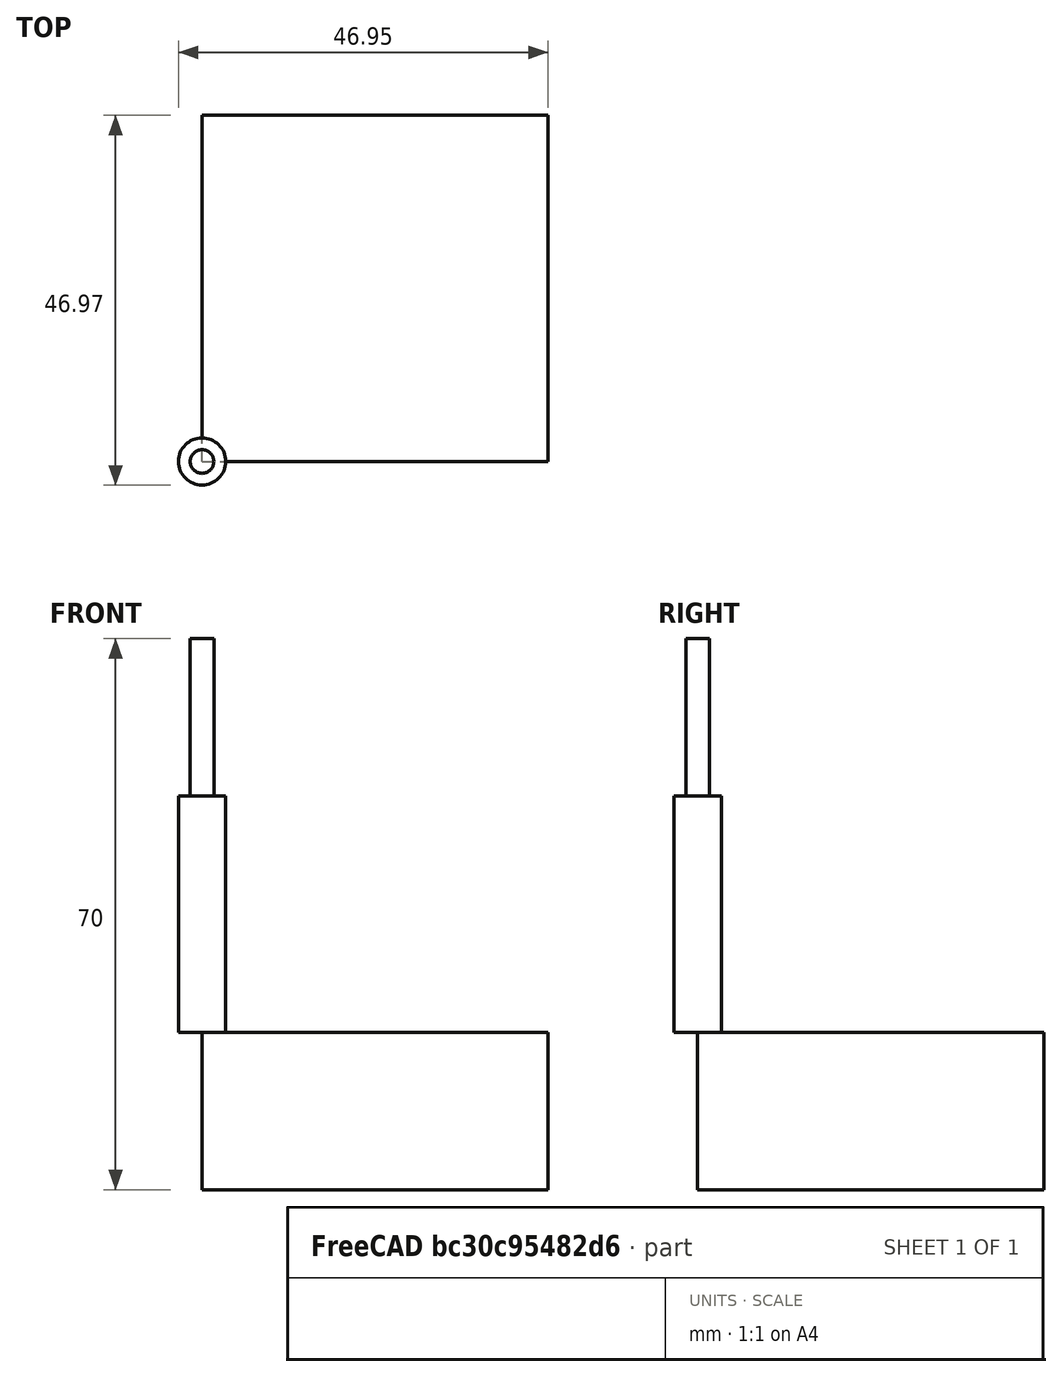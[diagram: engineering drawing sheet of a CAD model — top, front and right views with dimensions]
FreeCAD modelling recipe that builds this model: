
FCSTD DOCUMENT  (FreeCAD 0.19R24276 (Git))
Label: BouchonPourEchelleBateau
License: All rights reserved
LicenseURL: http://en.wikipedia.org/wiki/All_rights_reserved
objects: Path::FeaturePython×5, Part::FeaturePython×3, Sketcher::SketchObject×2, PartDesign::Pad×2, App::DocumentObjectGroup×2, PartDesign::Body×1, App::FeaturePython×1, Path::FeatureCompoundPython×1, Mesh::FeaturePython×1
note: 12 computed .brp shape members not serialized (recipe doc carries the construction recipe); baked Part::Feature solids carry a one-line shape summary decoded from their .brp

FEATURE [Sketcher::SketchObject] Sketch
  FullyConstrained = false
  MapMode = 5
  Support = -> [XY_Plane]
  sketch-geometry (1):
    g0: Circle CenterX=0 CenterY=0 CenterZ=0 NormalX=0 NormalY=0 NormalZ=1 AngleXU=0 Radius=12
  constraints (2):
    c: PointOnObject(g0,g-2)
    c: Radius(g0) = 12
FEATURE [PartDesign::Pad] Pad
  Direction = (1,1,1)
  Length = 4
  Length2 = 100
  Profile = -> Sketch
  Type = 0
FEATURE [Sketcher::SketchObject] Sketch001
  FullyConstrained = true
  MapMode = 5
  Placement = pos=(0,0,4) rot=(0,0,1;0rad)
  Support = -> [Pad]
  sketch-geometry (1):
    g0: Circle CenterX=0 CenterY=0 CenterZ=0 NormalX=0 NormalY=0 NormalZ=1 AngleXU=0 Radius=10
  constraints (2):
    c: Coincident(g0,g-1)
    c: Radius(g0) = 10
FEATURE [PartDesign::Pad] Pad001
  BaseFeature = -> Pad
  Direction = (1,1,1)
  Length = 16
  Length2 = 100
  Profile = -> Sketch001
  Type = 0
FEATURE [PartDesign::Body] Body
  Group = -> [Sketch,Pad,Sketch001,Pad001]
  Origin = -> Origin
  Tip = -> Pad001
FEATURE [App::FeaturePython] SetupSheet  # Path/CAM operation (typed FeaturePython)
  ClearanceHeightExpression = OpStockZMax+SetupSheet.ClearanceHeightOffset
  ClearanceHeightOffset = 5
  CoolantMode = 0
  CoolantModes = None | Flood | Mist
  FinalDepthExpression = OpFinalDepth
  HorizRapid = 0
  SafeHeightExpression = OpStockZMax+SetupSheet.SafeHeightOffset
  SafeHeightOffset = 3
  StartDepthExpression = OpStartDepth
  StepDownExpression = OpToolDiameter
  VertRapid = 0
FEATURE [Part::FeaturePython] Clone  label="Model-Body"  # Draft clone (typed FeaturePython)
  AttacherType = Attacher::AttachEngine3D
  Fuse = false
  Objects = -> [Body]
  PathResource = Model
  Placement = pos=(21.9457,21.9864,-20) rot=(0,0,1;0rad)
  Scale = (1,1,1)
FEATURE [App::DocumentObjectGroup] Model
  Group = -> [Clone]
FEATURE [Part::FeaturePython] ToolBit  label="Endmill"  # Path/CAM toolbit (typed FeaturePython)
  BitPropertyNames = Chipload | CuttingEdgeHeight | Diameter | Flutes | Length | Material | ShankDiameter
  BitShape = /Volumes/SSD/Applications/FreeCAD_0.19-24276.app/Contents/Resources/Mod/Path/Tools/Shape/endmill.fcstd
  Chipload = 0
  CuttingEdgeHeight = 30
  Diameter = 6
  Flutes = 0
  Length = 50
  Material = 0
  ShankDiameter = 3
  ShapeName = endmill
FEATURE [Path::FeaturePython] TC__Default_Tool  label="TC: Default Tool"  # Path/CAM operation (typed FeaturePython)
  HorizFeed = 0
  HorizRapid = 0
  SpindleDir = 0
  SpindleSpeed = 0
  Tool = -> ToolBit
  ToolNumber = 1
  VertFeed = 0
  VertRapid = 0
  expr: HorizRapid = SetupSheet.HorizRapid
  expr: VertRapid = SetupSheet.VertRapid
FEATURE [App::DocumentObjectGroup] Tools
  Group = -> [TC__Default_Tool]
FEATURE [Path::FeaturePython] Profile  # Path/CAM operation (typed FeaturePython)
  Active = true
  AreaParams:
    Tolerance = 1e-07
    FitArcs = True
    Simplify = False
    CleanDistance = 0.0
    Accuracy = 0.01
    Unit = 1.0
    MinArcPoints = 4
    MaxArcPoints = 100
    ClipperScale = 10000000.0
    Fill = 0
    Coplanar = 0
    Reorient = True
    Outline = False
    Explode = False
    OpenMode = 0
    Deflection = 0.01
    SubjectFill = 0
    ClipFill = 0
    Offset = 3.0
    ExtraPass = 0
    Stepover = 0.0
    LastStepover = 0.0
    JoinType = 0
    EndType = 0
    MiterLimit = 2.0
    RoundPrecision = 0.0
    PocketMode = 0
    ToolRadius = 1.0
    PocketExtraOffset = 0.0
    PocketStepover = 0.0
    PocketLastStepover = 0.0
    FromCenter = False
    Angle = 45.0
    AngleShift = 0.0
    Shift = 0.0
    Thicken = False
    SectionCount = -1
    Stepdown = 1.0
    SectionOffset = 0.0
    SectionTolerance = 1e-06
    SectionMode = 2
    Project = False
  AttemptInverseAngle = true
  Base = -> [Clone]
  ClearanceHeight = 5
  CoolantMode = None
  CycleTime = Cycletime Error
  Direction = 0
  EnableRotation = 0
  FinalDepth = -16
  HandleMultipleFeatures = 0
  InverseAngle = false
  JoinType = 0
  LimitDepthToFace = true
  MiterLimit = 0.1
  OffsetExtra = 0
  OpFinalDepth = -16
  OpStartDepth = 0
  OpStockZMax = 0
  OpStockZMin = -20
  OpToolDiameter = 6
  PathParams = {'orientation': 1, 'feedrate': 0.0, 'feedrate_v': 0.0, 'verbose': True, 'resume_height': 3.0, 'retraction': 5.0, 'return_end': True, 'preamble': False}
  ReverseDirection = false
  SafeHeight = 3
  Side = 0
  StartDepth = 0
  StartPoint = (0,0,0)
  StepDown = 4
  ToolController = -> TC__Default_Tool
  UseComp = true
  UseStartPoint = false
  processCircles = false
  processHoles = false
  processPerimeter = true
  expr: StepDown = 4
  expr: ClearanceHeight = OpStockZMax + SetupSheet.ClearanceHeightOffset
  expr: SafeHeight = OpStockZMax + SetupSheet.SafeHeightOffset
  expr: FinalDepth = -16
  expr: StartDepth = OpStartDepth
FEATURE [Part::FeaturePython] Stock001  # WARN: FeaturePython — macro-defined, semantics opaque (R4)
  Base = -> Model
  ExtXneg = 10
  ExtXpos = 10
  ExtYneg = 10
  ExtYpos = 10
  ExtZneg = 0
  ExtZpos = 0
  Placement = pos=(10,10,-20) rot=(0,0,1;0rad)
  StockType = FromBase
FEATURE [Path::FeaturePython] Profile001  # Path/CAM operation (typed FeaturePython)
  Active = true
  AreaParams:
    Tolerance = 1e-07
    FitArcs = True
    Simplify = False
    CleanDistance = 0.0
    Accuracy = 0.01
    Unit = 1.0
    MinArcPoints = 4
    MaxArcPoints = 100
    ClipperScale = 10000000.0
    Fill = 0
    Coplanar = 0
    Reorient = True
    Outline = False
    Explode = False
    OpenMode = 0
    Deflection = 0.01
    SubjectFill = 0
    ClipFill = 0
    Offset = 3.0
    ExtraPass = 0
    Stepover = 0.0
    LastStepover = 0.0
    JoinType = 0
    EndType = 0
    MiterLimit = 2.0
    RoundPrecision = 0.0
    PocketMode = 0
    ToolRadius = 1.0
    PocketExtraOffset = 0.0
    PocketStepover = 0.0
    PocketLastStepover = 0.0
    FromCenter = False
    Angle = 45.0
    AngleShift = 0.0
    Shift = 0.0
    Thicken = False
    SectionCount = -1
    Stepdown = 1.0
    SectionOffset = 0.0
    SectionTolerance = 1e-06
    SectionMode = 2
    Project = False
  AttemptInverseAngle = true
  Base = -> [Clone]
  ClearanceHeight = 5
  CoolantMode = None
  CycleTime = Cycletime Error
  Direction = 0
  EnableRotation = 0
  FinalDepth = -20
  HandleMultipleFeatures = 0
  InverseAngle = false
  JoinType = 0
  LimitDepthToFace = true
  MiterLimit = 0.1
  OffsetExtra = 0
  OpFinalDepth = -20
  OpStartDepth = 0
  OpStockZMax = 0
  OpStockZMin = -20
  OpToolDiameter = 6
  PathParams = {'orientation': 1, 'feedrate': 0.0, 'feedrate_v': 0.0, 'verbose': True, 'resume_height': 3.0, 'retraction': 5.0, 'return_end': True, 'preamble': False}
  ReverseDirection = false
  SafeHeight = 3
  Side = 0
  StartDepth = 0
  StartPoint = (0,0,0)
  StepDown = 4
  ToolController = -> TC__Default_Tool
  UseComp = true
  UseStartPoint = false
  processCircles = false
  processHoles = false
  processPerimeter = true
  expr: ClearanceHeight = OpStockZMax + SetupSheet.ClearanceHeightOffset
  expr: SafeHeight = OpStockZMax + SetupSheet.SafeHeightOffset
  expr: StepDown = 4
  expr: FinalDepth = OpFinalDepth
  expr: StartDepth = OpStartDepth
FEATURE [Path::FeaturePython] DressupTag  # Path/CAM operation (typed FeaturePython)
  Angle = 45
  Base = -> Profile001
  Height = 10
  Positions = (4) [(36.5556,25.3767,0),(31.4236,10.3626,0),(12.7651,10.1263,0),(10.0856,31.167,0)]
  Radius = 0
  SegmentationFactor = 50
  Width = 3.34
FEATURE [Path::FeatureCompoundPython] Operations  # Path/CAM operation (typed FeaturePython)
  Group = -> [Profile,DressupTag]
  UsePlacements = false
FEATURE [Path::FeaturePython] Job  # Path/CAM operation (typed FeaturePython)
  CycleTime = 00:00:00
  Fixtures = G54
  GeometryTolerance = 0.01
  LastPostProcessDate = 2021-04-19 23:07:09.662268
  LastPostProcessOutput = /Volumes/SSD/Dev/CNC/MiscCNC/BouchonPourEchelleBateau.gcode
  Model = -> Model
  Operations = -> Operations
  OrderOutputBy = 0
  PostProcessor = 1
  PostProcessorOutputFile = /Volumes/SSD/Dev/CNC/MiscCNC/BouchonPourEchelleBateau.gcode
  SetupSheet = -> SetupSheet
  SplitOutput = false
  Stock = -> Stock001
  Tools = -> Tools
FEATURE [Mesh::FeaturePython] CutMaterial  # WARN: FeaturePython — macro-defined, semantics opaque (R4)
